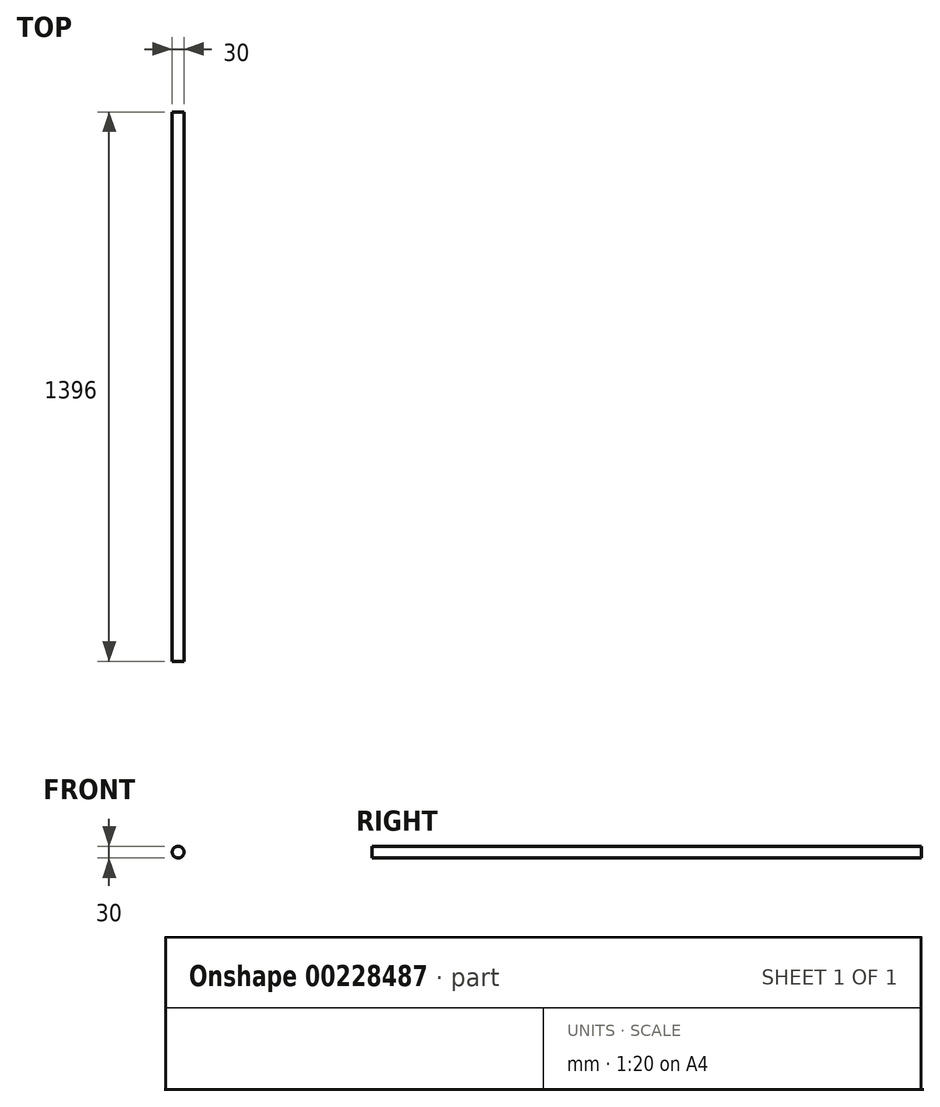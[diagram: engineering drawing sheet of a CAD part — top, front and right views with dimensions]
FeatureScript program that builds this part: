
annotation { "Feature Type Name" : "Feature", "Feature Type Description" : "" }
export const myFeature = defineFeature(function(context is Context, id is Id, definition is map)
    precondition{}
    {
        {
            var Q0;
            Q0=qCreatedBy(makeId("Front.planeOp"),FACE);
            var sketch = newSketch(context, id + "F0", { "sketchPlane" : qUnion([Q0])});
            skCircle(sketch, "E0", {"center": v(0, 0) * mm, "radius": 15 * mm});
            skSolve(sketch);
        }
        {
            var Q0;
            Q0 = qSketchRegion(id + "F0", true);
            extrude(context, id + "F1", {"entities" : qUnion([Q0]), "depth" : (1240 + 2 * 78) * mm, "offsetDistance" : 25 * mm, "symmetric" : true});
        }
    });
